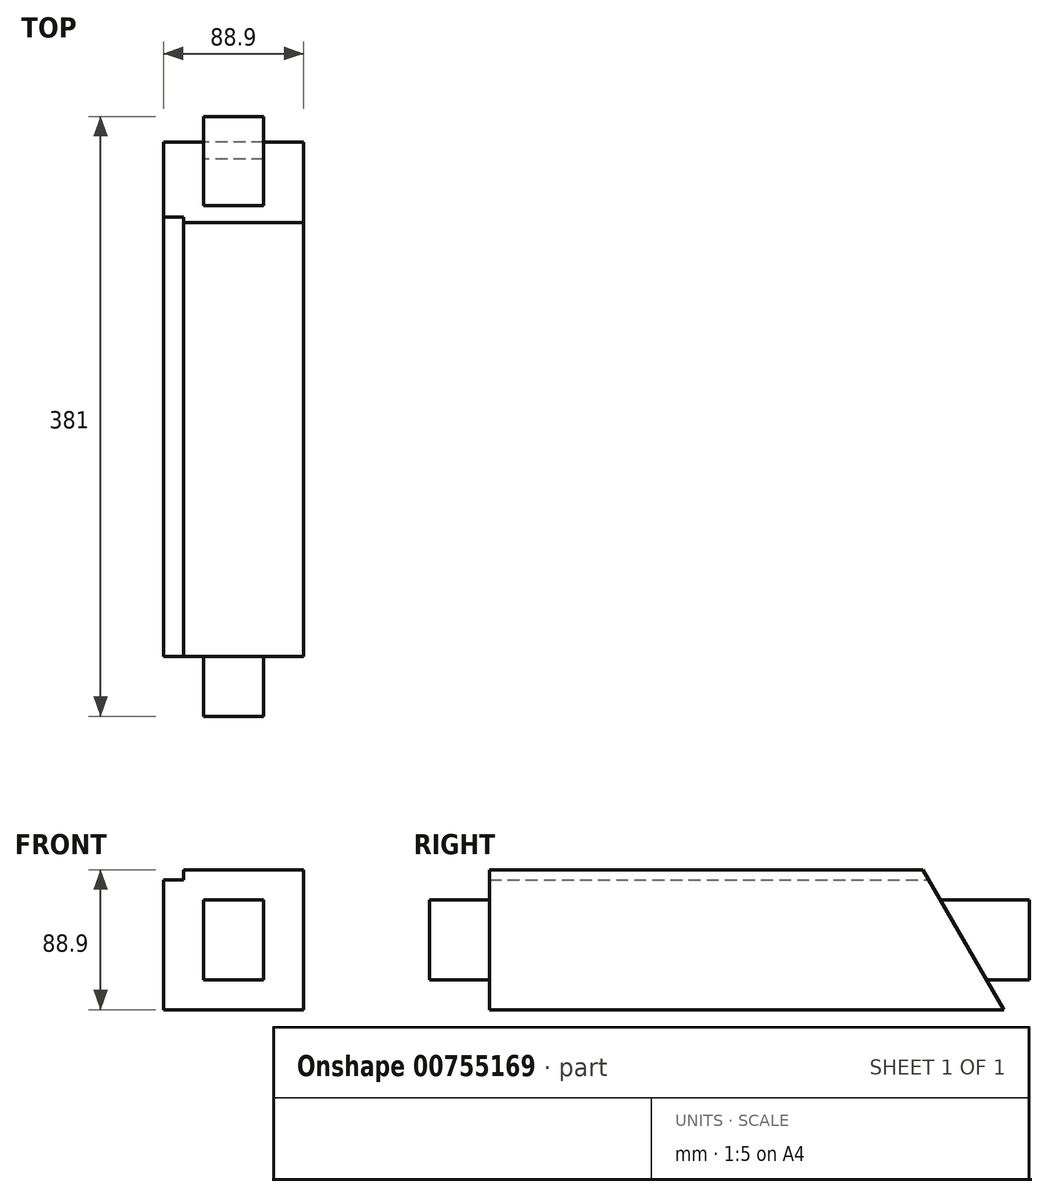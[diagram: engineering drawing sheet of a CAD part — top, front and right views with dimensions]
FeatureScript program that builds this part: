
annotation { "Feature Type Name" : "Feature", "Feature Type Description" : "" }
export const myFeature = defineFeature(function(context is Context, id is Id, definition is map)
    precondition{}
    {
        {
            var Q0;
            Q0=qCreatedBy(makeId("Right.planeOp"),FACE);
            var sketch = newSketch(context, id + "F0", { "sketchPlane" : qUnion([Q0])});
            skLineSegment(sketch, "E0.bottom", {"start": v(-190.5, 44.45) * mm, "end": v(190.5, 44.45) * mm});
            skLineSegment(sketch, "E0.top", {"start": v(-190.5, -44.45) * mm, "end": v(190.5, -44.45) * mm});
            skLineSegment(sketch, "E0.left", {"start": v(-190.5, 44.45) * mm, "end": v(-190.5, -44.45) * mm});
            skLineSegment(sketch, "E0.right", {"start": v(190.5, 44.45) * mm, "end": v(190.5, -44.45) * mm});
            skPoint(sketch, "E0.middle", {"position": v(0, 0) * mm});
            skSolve(sketch);
        }
        {
            var Q0;
            Q0 = qSketchRegion(id + "F0", true);
            extrude(context, id + "F1", {"entities" : qUnion([Q0]), "endBound" : BoundingType.SYMMETRIC, "depth" : 88.9 * mm, "offsetDistance" : 25.4 * mm});
        }
        {
            var Q0;
            Q0=makeQuery(id+"F1.opExtrude","SWEPT_FACE",FACE,{"disambiguationData":[OSD([sQuery(id+"F0.wireOp",EDGE,"E0.bottom")])]});
            var sketch = newSketch(context, id + "F2", { "sketchPlane" : qUnion([Q0])});
            skLineSegment(sketch, "E1", {"start": v(44.45, 122.94) * mm, "end": v(-44.45, 122.94) * mm, "construction": true});
            skSolve(sketch);
        }
        {
            var Q0;
            Q0=sQuery(id+"F2.wireOp",EDGE,"E1");
            cPlane(context, id + "F3", {"entities" : qUnion([Q0]), "cplaneType" : CPlaneType.LINE_ANGLE, "offset" : 25.4 * mm, "angle" : 30 * degree, "oppositeDirection" : true, "width" : 152.4 * mm, "height" : 152.4 * mm});
        }
        {
            var Q0;
            Q0=makeQuery(id+"F1.opExtrude","SWEPT_FACE",FACE,{"disambiguationData":[OSD([sQuery(id+"F0.wireOp",EDGE,"E0.right")])]});
            var sketch = newSketch(context, id + "F4", { "sketchPlane" : qUnion([Q0])});
            skLineSegment(sketch, "E2.bottom", {"start": v(-44.45, 44.45) * mm, "end": v(44.45, 44.45) * mm});
            skLineSegment(sketch, "E2.top", {"start": v(-44.45, -44.45) * mm, "end": v(44.45, -44.45) * mm});
            skLineSegment(sketch, "E2.left", {"start": v(-44.45, 44.45) * mm, "end": v(-44.45, -44.45) * mm});
            skLineSegment(sketch, "E2.right", {"start": v(44.45, 44.45) * mm, "end": v(44.45, -44.45) * mm});
            skPoint(sketch, "E2.middle", {"position": v(0, 0) * mm});
            skLineSegment(sketch, "E3.bottom", {"start": v(-19.05, 25.4) * mm, "end": v(19.05, 25.4) * mm});
            skLineSegment(sketch, "E3.top", {"start": v(-19.05, -25.4) * mm, "end": v(19.05, -25.4) * mm});
            skLineSegment(sketch, "E3.left", {"start": v(-19.05, 25.4) * mm, "end": v(-19.05, -25.4) * mm});
            skLineSegment(sketch, "E3.right", {"start": v(19.05, 25.4) * mm, "end": v(19.05, -25.4) * mm});
            skSolve(sketch);
        }
        {
            var Q0;
            Q0=makeQuery(id+"F4.imprint","IMPRINT",FACE,{"disambiguationData":[TD([[makeQuery(id+"F4.imprint","IMPRINT",EDGE,{"derivedFrom":sQuery(id+"F4.wireOp",EDGE,"E2.bottom")}),-1.0]])]});
            var sketch = newSketch(context, id + "F5", { "sketchPlane" : qUnion([Q0])});
            skLineSegment(sketch, "E4.bottom", {"start": v(44.45, 44.45) * mm, "end": v(31.75, 44.45) * mm});
            skLineSegment(sketch, "E4.top", {"start": v(44.45, 38.1) * mm, "end": v(31.75, 38.1) * mm});
            skLineSegment(sketch, "E4.left", {"start": v(44.45, 44.45) * mm, "end": v(44.45, 38.1) * mm});
            skLineSegment(sketch, "E4.right", {"start": v(31.75, 44.45) * mm, "end": v(31.75, 38.1) * mm});
            skSolve(sketch);
        }
        {
            var Q0;
            Q0 = qSketchRegion(id + "F5", true);
            extrude(context, id + "F6", {"entities" : qUnion([Q0]), "operationType" : NewBodyOperationType.REMOVE, "endBound" : BoundingType.THROUGH_ALL, "oppositeDirection" : true, "depth" : 25.4 * mm, "offsetDistance" : 25.4 * mm});
        }
        {
            var Q0;
            Q0 = qSketchRegion(id + "F4", true);
            var Q1;
            Q1=qCreatedBy(id+"F3.planeOp",FACE);
            extrude(context, id + "F7", {"entities" : qUnion([Q0]), "operationType" : NewBodyOperationType.REMOVE, "endBound" : BoundingType.UP_TO_SURFACE, "oppositeDirection" : true, "depth" : 25.4 * mm, "endBoundEntityFace" : qUnion([Q1]), "offsetDistance" : 25.4 * mm});
        }
        {
            var Q0;
            Q0=makeQuery(id+"F1.opExtrude","SWEPT_FACE",FACE,{"disambiguationData":[OSD([sQuery(id+"F0.wireOp",EDGE,"E0.left")])]});
            var sketch = newSketch(context, id + "F8", { "sketchPlane" : qUnion([Q0])});
            skLineSegment(sketch, "E5.bottom", {"start": v(-44.45, 44.45) * mm, "end": v(44.45, 44.45) * mm});
            skLineSegment(sketch, "E5.top", {"start": v(-44.45, -44.45) * mm, "end": v(44.45, -44.45) * mm});
            skLineSegment(sketch, "E5.left", {"start": v(-44.45, 44.45) * mm, "end": v(-44.45, -44.45) * mm});
            skLineSegment(sketch, "E5.right", {"start": v(44.45, 44.45) * mm, "end": v(44.45, -44.45) * mm});
            skPoint(sketch, "E5.middle", {"position": v(0, 0) * mm});
            skLineSegment(sketch, "E6.bottom", {"start": v(-19.05, 25.4) * mm, "end": v(19.05, 25.4) * mm});
            skLineSegment(sketch, "E6.top", {"start": v(-19.05, -25.4) * mm, "end": v(19.05, -25.4) * mm});
            skLineSegment(sketch, "E6.left", {"start": v(-19.05, 25.4) * mm, "end": v(-19.05, -25.4) * mm});
            skLineSegment(sketch, "E6.right", {"start": v(19.05, 25.4) * mm, "end": v(19.05, -25.4) * mm});
            skSolve(sketch);
        }
        {
            var Q0;
            Q0 = qSketchRegion(id + "F8", true);
            extrude(context, id + "F9", {"entities" : qUnion([Q0]), "operationType" : NewBodyOperationType.REMOVE, "oppositeDirection" : true, "depth" : 38.1 * mm, "offsetDistance" : 25.4 * mm});
        }
    });
